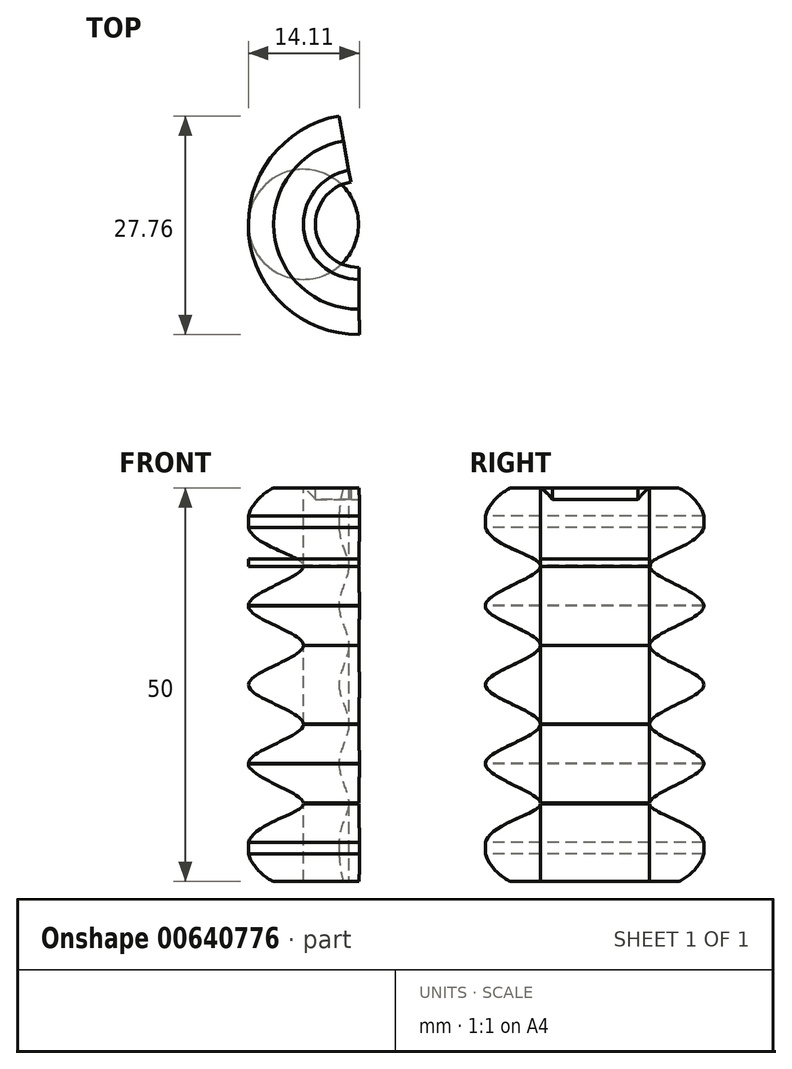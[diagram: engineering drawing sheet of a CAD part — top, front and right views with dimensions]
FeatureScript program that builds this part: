
annotation { "Feature Type Name" : "Feature", "Feature Type Description" : "" }
export const myFeature = defineFeature(function(context is Context, id is Id, definition is map)
    precondition{}
    {
        {
            var Q0;
            Q0=qCreatedBy(makeId("Front.planeOp"),FACE);
            var sketch = newSketch(context, id + "F0", { "sketchPlane" : qUnion([Q0])});
            skLineSegment(sketch, "E0", {"start": v(0, 10) * mm, "end": v(-7, 10) * mm});
            skLineSegment(sketch, "E1", {"start": v(-7, 10) * mm, "end": v(-7, -15) * mm});
            skLineSegment(sketch, "E2", {"start": v(-7, -15) * mm, "end": v(0, -15) * mm});
            skLineSegment(sketch, "E3", {"start": v(-7, 10) * mm, "end": v(-7, 5) * mm});
            skLineSegment(sketch, "E4", {"start": v(-7, 5) * mm, "end": v(-7, 0) * mm});
            skLineSegment(sketch, "E5", {"start": v(-7, 0) * mm, "end": v(-7, -5) * mm});
            skLineSegment(sketch, "E6", {"start": v(-7, -5) * mm, "end": v(-7, -10) * mm});
            skLineSegment(sketch, "E7", {"start": v(-7, 5) * mm, "end": v(0, 5) * mm});
            skLineSegment(sketch, "E8", {"start": v(-7, 0) * mm, "end": v(0, 0) * mm});
            skLineSegment(sketch, "E9", {"start": v(-7, -5) * mm, "end": v(0, -5) * mm});
            skLineSegment(sketch, "E10", {"start": v(-7, -10) * mm, "end": v(0, -10) * mm});
            skLineSegment(sketch, "E11.top", {"start": v(-7, -20) * mm, "end": v(0, -20) * mm});
            skLineSegment(sketch, "E11.left", {"start": v(-7, -15) * mm, "end": v(-7, -20) * mm});
            skLineSegment(sketch, "E11.right", {"start": v(0, -15) * mm, "end": v(0, -20) * mm});
            skLineSegment(sketch, "E12", {"start": v(0, 10) * mm, "end": v(0, -20) * mm});
            skLineSegment(sketch, "E13.top", {"start": v(-7, -25) * mm, "end": v(0, -25) * mm});
            skLineSegment(sketch, "E13.left", {"start": v(-7, -20) * mm, "end": v(-7, -25) * mm});
            skLineSegment(sketch, "E13.right", {"start": v(0, -20) * mm, "end": v(0, -25) * mm});
            skLineSegment(sketch, "E14.top", {"start": v(-7, -30) * mm, "end": v(0, -30) * mm});
            skLineSegment(sketch, "E14.left", {"start": v(-7, -25) * mm, "end": v(-7, -30) * mm});
            skLineSegment(sketch, "E14.right", {"start": v(0, -25) * mm, "end": v(0, -30) * mm});
            skLineSegment(sketch, "E15.top", {"start": v(-7, -35) * mm, "end": v(0, -35) * mm});
            skLineSegment(sketch, "E15.left", {"start": v(-7, -30) * mm, "end": v(-7, -35) * mm});
            skLineSegment(sketch, "E15.right", {"start": v(0, -30) * mm, "end": v(0, -35) * mm});
            skLineSegment(sketch, "E16.top", {"start": v(-7, -40) * mm, "end": v(0, -40) * mm});
            skLineSegment(sketch, "E16.left", {"start": v(-7, -35) * mm, "end": v(-7, -40) * mm});
            skLineSegment(sketch, "E16.right", {"start": v(0, -35) * mm, "end": v(0, -40) * mm});
            skFitSpline(sketch, "E17", {"points": [v(0, 10) * mm, v(-7, 5) * mm, v(0, 0) * mm, v(-7, -5) * mm, v(0, -10) * mm, v(-7, -15) * mm, v(0, -20) * mm, v(-7, -25) * mm, v(0, -30) * mm, v(-7, -35) * mm, v(0, -40) * mm, v(0, 10) * mm]});
            skLineSegment(sketch, "E18.bottom", {"start": v(0, 10) * mm, "end": v(1.52, 10) * mm});
            skLineSegment(sketch, "E18.top", {"start": v(0, -40.03) * mm, "end": v(1.52, -40.03) * mm});
            skLineSegment(sketch, "E18.left", {"start": v(0, 10) * mm, "end": v(0, -40.03) * mm});
            skLineSegment(sketch, "E18.right", {"start": v(1.52, 10) * mm, "end": v(1.52, -40.03) * mm});
            skSolve(sketch);
        }
        {
            var Q0;
            Q0=qCreatedBy(makeId("Top.planeOp"),FACE);
            var sketch = newSketch(context, id + "F1", { "sketchPlane" : qUnion([Q0])});
            skCircle(sketch, "E19", {"center": v(0, 0) * mm, "radius": 7 * mm});
            skSolve(sketch);
        }
        {
            var Q0;
            Q0=makeQuery(id+"F1.imprint","IMPRINT",FACE,{"disambiguationData":[TD([[makeQuery(id+"F1.imprint","IMPRINT",EDGE,{"derivedFrom":sQuery(id+"F1.wireOp",EDGE,"E19")}),1.0]])]});
            extrude(context, id + "F2", {"entities" : qUnion([Q0]), "depth" : 1 * mm, "offsetDistance" : 25 * mm});
        }
        {
            var Q0;
            Q0=makeQuery(id+"F2.opExtrude","CAP_FACE",FACE,{"disambiguationData":[OSD([sQuery(id+"F1.wireOp",EDGE,"E19")])],"isStart":false});
            var sketch = newSketch(context, id + "F3", { "sketchPlane" : qUnion([Q0])});
            skArc(sketch, "E20", {"start": v(4.95, 11.38) * mm, "mid": v(-4.52, -1.07) * mm, "end": v(7.09, -11.56) * mm});
            skPoint(sketch, "E21", {"position": v(4.95, 11.38) * mm});
            skPoint(sketch, "E22", {"position": v(7.09, -11.56) * mm});
            skSolve(sketch);
        }
        {
            var Q0;
            {var subQ2=sQuery(id+"F0.wireOp",EDGE,"E15.top");Q0=makeQuery(id+"F0.imprint","IMPRINT",FACE,{"disambiguationData":[TD([[makeQuery(id+"F0.imprint","IMPRINT",EDGE,{"derivedFrom":subQ2}),-1.0]])]});}
            var Q1;
            {var subQ0=sQuery(id+"F0.wireOp",EDGE,"E15.top");Q1=makeQuery(id+"F0.imprint","IMPRINT",FACE,{"disambiguationData":[TD([[makeQuery(id+"F0.imprint","IMPRINT",EDGE,{"derivedFrom":subQ0}),1.0]])]});}
            var Q2;
            {var subQ0=sQuery(id+"F0.wireOp",EDGE,"E13.top");Q2=makeQuery(id+"F0.imprint","IMPRINT",FACE,{"disambiguationData":[TD([[makeQuery(id+"F0.imprint","IMPRINT",EDGE,{"derivedFrom":subQ0}),-1.0]])]});}
            var Q3;
            {var subQ0=sQuery(id+"F0.wireOp",EDGE,"E13.right");Q3=makeQuery(id+"F0.imprint","IMPRINT",FACE,{"disambiguationData":[TD([[makeQuery(id+"F0.imprint","IMPRINT",EDGE,{"derivedFrom":subQ0}),-1.0]])]});}
            var Q4;
            {var subQ0=sQuery(id+"F0.wireOp",EDGE,"E2");Q4=makeQuery(id+"F0.imprint","IMPRINT",FACE,{"disambiguationData":[TD([[makeQuery(id+"F0.imprint","IMPRINT",EDGE,{"derivedFrom":subQ0}),-1.0]])]});}
            var Q5;
            {var subQ0=sQuery(id+"F0.wireOp",EDGE,"E2");Q5=makeQuery(id+"F0.imprint","IMPRINT",FACE,{"disambiguationData":[TD([[makeQuery(id+"F0.imprint","IMPRINT",EDGE,{"derivedFrom":subQ0}),1.0]])]});}
            var Q6;
            {var subQ0=sQuery(id+"F0.wireOp",EDGE,"E9");Q6=makeQuery(id+"F0.imprint","IMPRINT",FACE,{"disambiguationData":[TD([[makeQuery(id+"F0.imprint","IMPRINT",EDGE,{"derivedFrom":subQ0}),-1.0]])]});}
            var Q7;
            {var subQ1=sQuery(id+"F0.wireOp",EDGE,"E9");Q7=makeQuery(id+"F0.imprint","IMPRINT",FACE,{"disambiguationData":[TD([[makeQuery(id+"F0.imprint","IMPRINT",EDGE,{"derivedFrom":subQ1}),1.0]])]});}
            var Q8;
            {var subQ0=sQuery(id+"F0.wireOp",EDGE,"E7");Q8=makeQuery(id+"F0.imprint","IMPRINT",FACE,{"disambiguationData":[TD([[makeQuery(id+"F0.imprint","IMPRINT",EDGE,{"derivedFrom":subQ0}),1.0]])]});}
            var Q9;
            {var subQ0=sQuery(id+"F0.wireOp",EDGE,"E7");Q9=makeQuery(id+"F0.imprint","IMPRINT",FACE,{"disambiguationData":[TD([[makeQuery(id+"F0.imprint","IMPRINT",EDGE,{"derivedFrom":subQ0}),-1.0]])]});}
            var Q10;
            {var subQ9=sQuery(id+"F0.wireOp",EDGE,"E18.bottom");Q10=makeQuery(id+"F0.imprint","IMPRINT",FACE,{"disambiguationData":[TD([[makeQuery(id+"F0.imprint","IMPRINT",EDGE,{"derivedFrom":subQ9}),-1.0]])]});}
            var Q11;
            {var subQ0=sQuery(id+"F0.wireOp",EDGE,"E13.top");Q11=makeQuery(id+"F0.imprint","IMPRINT",FACE,{"disambiguationData":[TD([[makeQuery(id+"F0.imprint","IMPRINT",EDGE,{"derivedFrom":subQ0}),1.0]])]});}
            var Q12;
            Q12=sQuery(id+"F3.wireOp",EDGE,"E20");
            sweep(context, id + "F4", {"profiles" : qUnion([Q0, Q1, Q2, Q3, Q4, Q5, Q6, Q7, Q8, Q9, Q10, Q11]), "path" : qUnion([Q12])});
        }
    });
